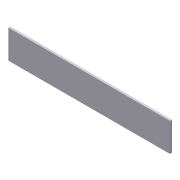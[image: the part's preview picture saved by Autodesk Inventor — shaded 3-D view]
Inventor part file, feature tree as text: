
AUTODESK INVENTOR PART (.ipt)
format: ipt  version: 2012 (Build 160160000, 160)  size: 59,904 bytes
history: native  units: in
note: dims shown in document units (in); Inventor stores cm internally (conversion verified against a paired STEP export)
features: extrude x1, sketch x1
ambient origin geometry x8: Origin, YZ Plane, XZ Plane, XY Plane, X Axis, Y Axis, Z Axis, Center Point
bodies: Solid1 (feature_tree)
feature tree (2):
  extrude  "Extrusion1"  Depth=19.75in
  sketch  "Sketch1"  dims[d0=3.5in d1=19.75in d2=0.25in d3=0.0in]
